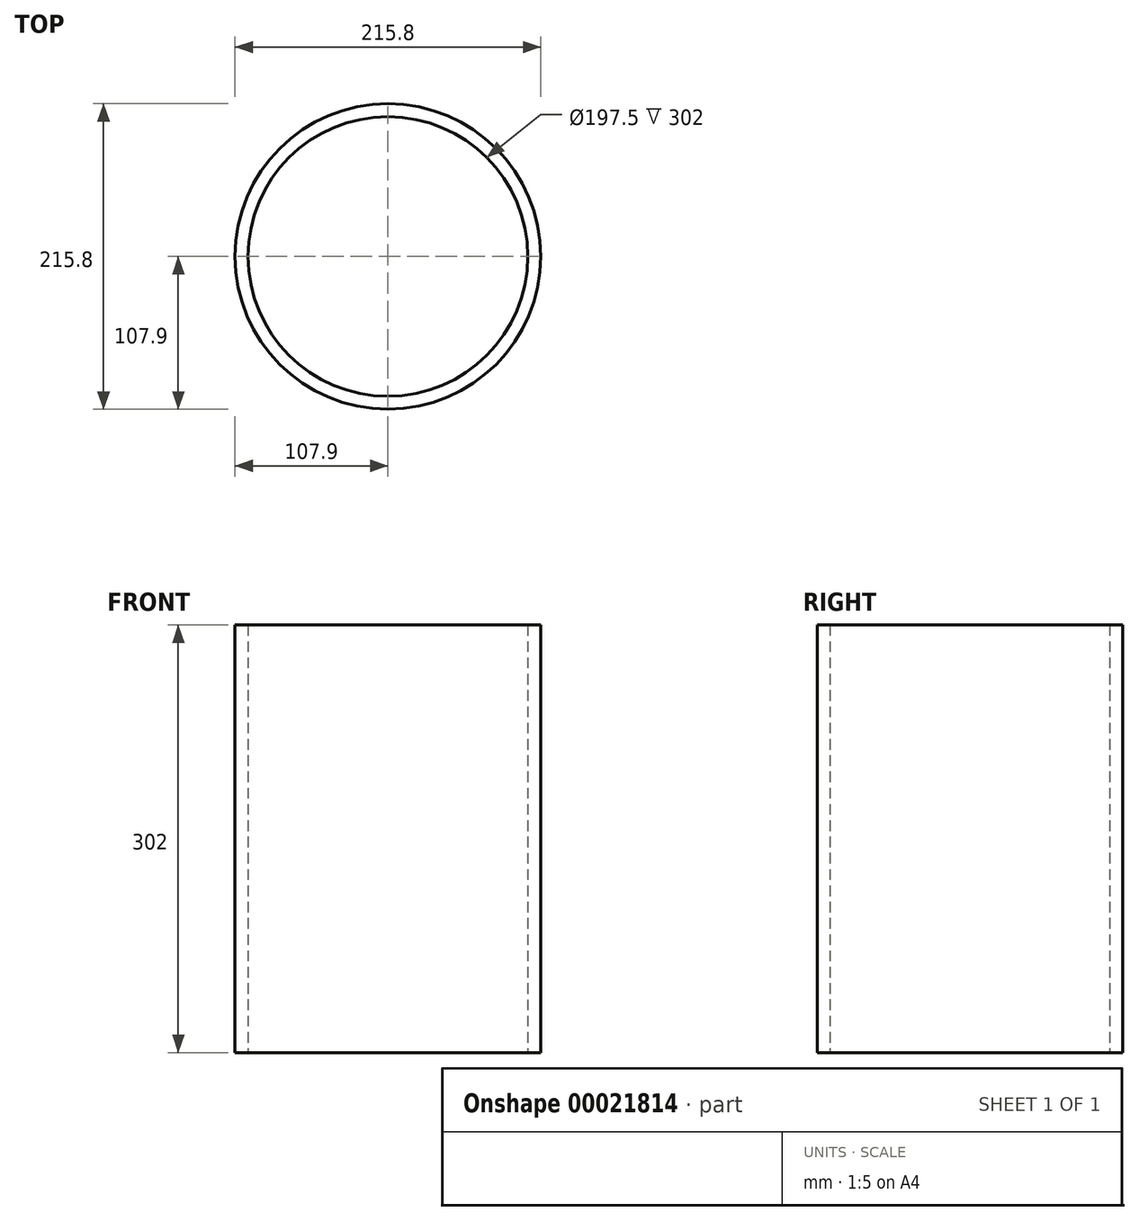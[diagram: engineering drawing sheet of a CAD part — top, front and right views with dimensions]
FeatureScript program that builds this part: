
annotation { "Feature Type Name" : "Feature", "Feature Type Description" : "" }
export const myFeature = defineFeature(function(context is Context, id is Id, definition is map)
    precondition{}
    {
        {
            var Q0;
            Q0=qCreatedBy(makeId("Top.planeOp"),FACE);
            var sketch = newSketch(context, id + "F0", { "sketchPlane" : qUnion([Q0])});
            skCircle(sketch, "E0", {"center": v(0, 0) * mm, "radius": 107.9 * mm});
            skCircle(sketch, "E1", {"center": v(0, 0) * mm, "radius": 98.75 * mm});
            skSolve(sketch);
        }
        {
            var Q0;
            Q0 = qSketchRegion(id + "F0", true);
            extrude(context, id + "F1", {"entities" : qUnion([Q0]), "depth" : 302 * mm});
        }
    });
